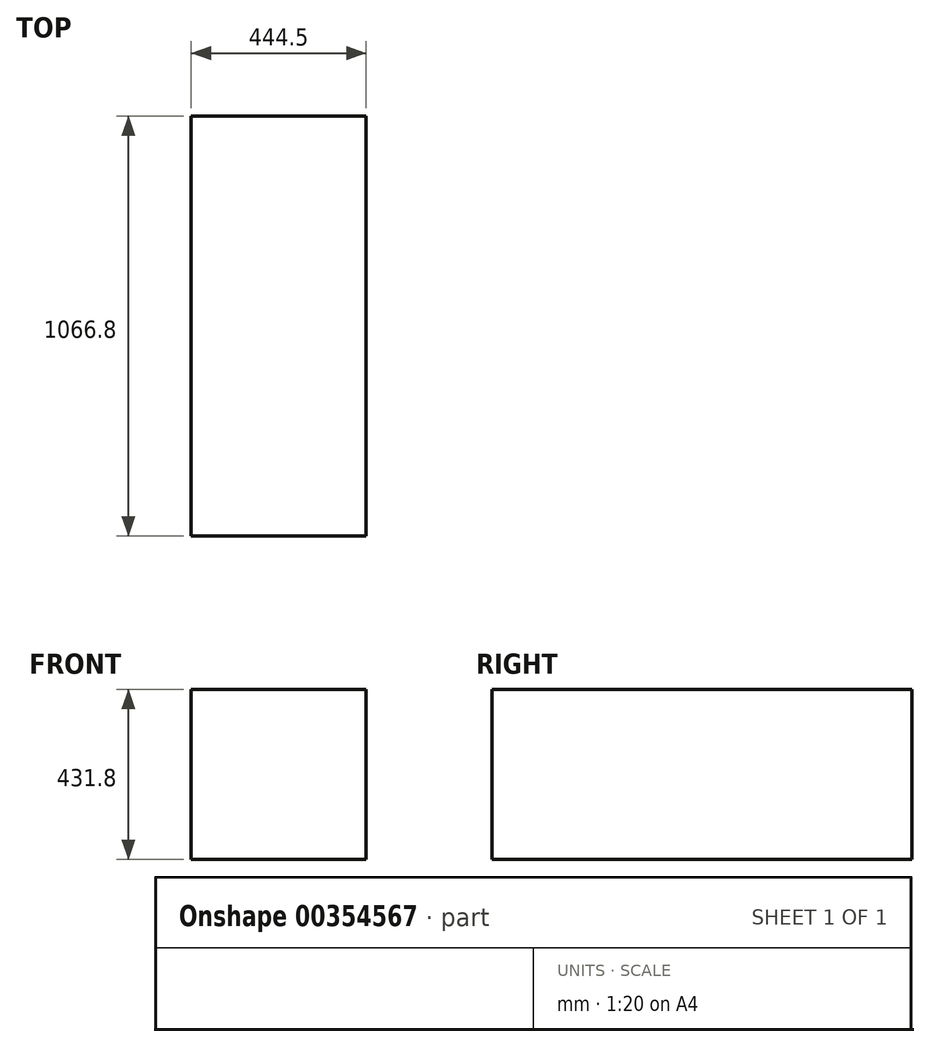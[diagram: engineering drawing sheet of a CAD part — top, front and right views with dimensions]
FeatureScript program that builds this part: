
annotation { "Feature Type Name" : "Feature", "Feature Type Description" : "" }
export const myFeature = defineFeature(function(context is Context, id is Id, definition is map)
    precondition{}
    {
        {
            var Q0;
            Q0=qCreatedBy(makeId("Top.planeOp"),FACE);
            var sketch = newSketch(context, id + "F0", { "sketchPlane" : qUnion([Q0])});
            skLineSegment(sketch, "E0.bottom", {"start": v(222.25, 533.4) * mm, "end": v(-222.25, 533.4) * mm});
            skLineSegment(sketch, "E0.top", {"start": v(222.25, -533.4) * mm, "end": v(-222.25, -533.4) * mm});
            skLineSegment(sketch, "E0.left", {"start": v(222.25, 533.4) * mm, "end": v(222.25, -533.4) * mm});
            skLineSegment(sketch, "E0.right", {"start": v(-222.25, 533.4) * mm, "end": v(-222.25, -533.4) * mm});
            skPoint(sketch, "E0.middle", {"position": v(0, 0) * mm});
            skSolve(sketch);
        }
        {
            var Q0;
            Q0=makeQuery(id+"F0.imprint","IMPRINT",FACE,{"disambiguationData":[TD([[makeQuery(id+"F0.imprint","IMPRINT",EDGE,{"derivedFrom":sQuery(id+"F0.wireOp",EDGE,"E0.bottom")}),1.0]])]});
            extrude(context, id + "F1", {"entities" : qUnion([Q0]), "depth" : 431.8 * mm});
        }
    });
